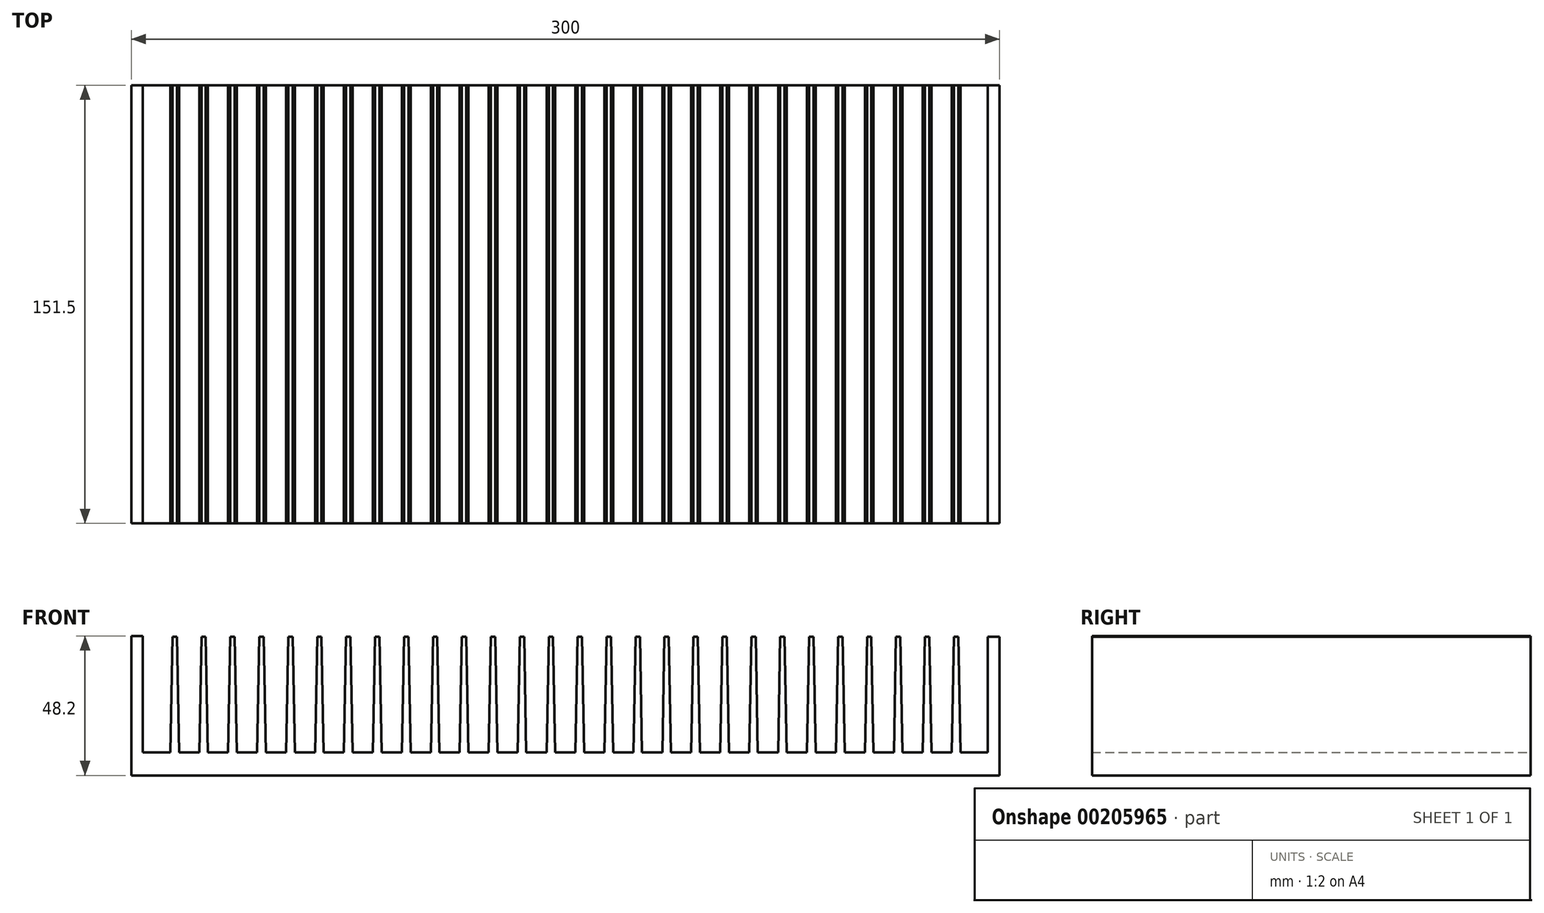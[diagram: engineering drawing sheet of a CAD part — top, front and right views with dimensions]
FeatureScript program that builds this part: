
annotation { "Feature Type Name" : "Feature", "Feature Type Description" : "" }
export const myFeature = defineFeature(function(context is Context, id is Id, definition is map)
    precondition{}
    {
        {
            var Q0;
            Q0=qCreatedBy(makeId("Front.planeOp"),FACE);
            var sketch = newSketch(context, id + "F0", { "sketchPlane" : qUnion([Q0])});
            skLineSegment(sketch, "E0", {"start": v(0, 0) * mm, "end": v(11.17, 0) * mm, "construction": true});
            skLineSegment(sketch, "E1", {"start": v(0, 0) * mm, "end": v(0, 12.82) * mm, "construction": true});
            skLineSegment(sketch, "E2", {"start": v(0, 48) * mm, "end": v(0.75, 48) * mm});
            skLineSegment(sketch, "E3", {"start": v(0.75, 48) * mm, "end": v(1.5, 8) * mm});
            skLineSegment(sketch, "E4", {"start": v(1.5, 8) * mm, "end": v(8.5, 8) * mm});
            skLineSegment(sketch, "E5", {"start": v(8.5, 8) * mm, "end": v(9.25, 48) * mm});
            skLineSegment(sketch, "E6", {"start": v(5, 23.61) * mm, "end": v(5, 0) * mm, "construction": true});
            skPoint(sketch, "E6.startSnap0", {"position": v(5, 8) * mm});
            skLineSegment(sketch, "E7", {"start": v(9.25, 48) * mm, "end": v(10, 48) * mm});
            skLineSegment(sketch, "E8.1.0.0", {"start": v(11.5, 8) * mm, "end": v(18.5, 8) * mm});
            skLineSegment(sketch, "E8.1.0.1", {"start": v(18.5, 8) * mm, "end": v(19.25, 48) * mm});
            skLineSegment(sketch, "E8.1.0.2", {"start": v(10.75, 48) * mm, "end": v(11.5, 8) * mm});
            skPoint(sketch, "E8.1.0.3", {"position": v(15, 8) * mm});
            skLineSegment(sketch, "E8.1.0.4", {"start": v(10, 48) * mm, "end": v(10.75, 48) * mm});
            skLineSegment(sketch, "E8.1.0.5", {"start": v(19.25, 48) * mm, "end": v(20, 48) * mm});
            skLineSegment(sketch, "E8.2.0.0", {"start": v(21.5, 8) * mm, "end": v(28.5, 8) * mm});
            skLineSegment(sketch, "E8.2.0.1", {"start": v(28.5, 8) * mm, "end": v(29.25, 48) * mm});
            skLineSegment(sketch, "E8.2.0.2", {"start": v(20.75, 48) * mm, "end": v(21.5, 8) * mm});
            skPoint(sketch, "E8.2.0.3", {"position": v(25, 8) * mm});
            skLineSegment(sketch, "E8.2.0.4", {"start": v(20, 48) * mm, "end": v(20.75, 48) * mm});
            skLineSegment(sketch, "E8.2.0.5", {"start": v(29.25, 48) * mm, "end": v(30, 48) * mm});
            skLineSegment(sketch, "E8.3.0.0", {"start": v(31.5, 8) * mm, "end": v(38.5, 8) * mm});
            skLineSegment(sketch, "E8.3.0.1", {"start": v(38.5, 8) * mm, "end": v(39.25, 48) * mm});
            skLineSegment(sketch, "E8.3.0.2", {"start": v(30.75, 48) * mm, "end": v(31.5, 8) * mm});
            skPoint(sketch, "E8.3.0.3", {"position": v(35, 8) * mm});
            skLineSegment(sketch, "E8.3.0.4", {"start": v(30, 48) * mm, "end": v(30.75, 48) * mm});
            skLineSegment(sketch, "E8.3.0.5", {"start": v(39.25, 48) * mm, "end": v(40, 48) * mm});
            skLineSegment(sketch, "E8.4.0.0", {"start": v(41.5, 8) * mm, "end": v(48.5, 8) * mm});
            skLineSegment(sketch, "E8.4.0.1", {"start": v(48.5, 8) * mm, "end": v(49.25, 48) * mm});
            skLineSegment(sketch, "E8.4.0.2", {"start": v(40.75, 48) * mm, "end": v(41.5, 8) * mm});
            skPoint(sketch, "E8.4.0.3", {"position": v(45, 8) * mm});
            skLineSegment(sketch, "E8.4.0.4", {"start": v(40, 48) * mm, "end": v(40.75, 48) * mm});
            skLineSegment(sketch, "E8.4.0.5", {"start": v(49.25, 48) * mm, "end": v(50, 48) * mm});
            skLineSegment(sketch, "E8.5.0.0", {"start": v(51.5, 8) * mm, "end": v(58.5, 8) * mm});
            skLineSegment(sketch, "E8.5.0.1", {"start": v(58.5, 8) * mm, "end": v(59.25, 48) * mm});
            skLineSegment(sketch, "E8.5.0.2", {"start": v(50.75, 48) * mm, "end": v(51.5, 8) * mm});
            skPoint(sketch, "E8.5.0.3", {"position": v(55, 8) * mm});
            skLineSegment(sketch, "E8.5.0.4", {"start": v(50, 48) * mm, "end": v(50.75, 48) * mm});
            skLineSegment(sketch, "E8.5.0.5", {"start": v(59.25, 48) * mm, "end": v(60, 48) * mm});
            skLineSegment(sketch, "E8.6.0.0", {"start": v(61.5, 8) * mm, "end": v(68.5, 8) * mm});
            skLineSegment(sketch, "E8.6.0.1", {"start": v(68.5, 8) * mm, "end": v(69.25, 48) * mm});
            skLineSegment(sketch, "E8.6.0.2", {"start": v(60.75, 48) * mm, "end": v(61.5, 8) * mm});
            skPoint(sketch, "E8.6.0.3", {"position": v(65, 8) * mm});
            skLineSegment(sketch, "E8.6.0.4", {"start": v(60, 48) * mm, "end": v(60.75, 48) * mm});
            skLineSegment(sketch, "E8.6.0.5", {"start": v(69.25, 48) * mm, "end": v(70, 48) * mm});
            skLineSegment(sketch, "E8.7.0.0", {"start": v(71.5, 8) * mm, "end": v(78.5, 8) * mm});
            skLineSegment(sketch, "E8.7.0.1", {"start": v(78.5, 8) * mm, "end": v(79.25, 48) * mm});
            skLineSegment(sketch, "E8.7.0.2", {"start": v(70.75, 48) * mm, "end": v(71.5, 8) * mm});
            skPoint(sketch, "E8.7.0.3", {"position": v(75, 8) * mm});
            skLineSegment(sketch, "E8.7.0.4", {"start": v(70, 48) * mm, "end": v(70.75, 48) * mm});
            skLineSegment(sketch, "E8.7.0.5", {"start": v(79.25, 48) * mm, "end": v(80, 48) * mm});
            skLineSegment(sketch, "E8.8.0.0", {"start": v(81.5, 8) * mm, "end": v(88.5, 8) * mm});
            skLineSegment(sketch, "E8.8.0.1", {"start": v(88.5, 8) * mm, "end": v(89.25, 48) * mm});
            skLineSegment(sketch, "E8.8.0.2", {"start": v(80.75, 48) * mm, "end": v(81.5, 8) * mm});
            skPoint(sketch, "E8.8.0.3", {"position": v(85, 8) * mm});
            skLineSegment(sketch, "E8.8.0.4", {"start": v(80, 48) * mm, "end": v(80.75, 48) * mm});
            skLineSegment(sketch, "E8.8.0.5", {"start": v(89.25, 48) * mm, "end": v(90, 48) * mm});
            skLineSegment(sketch, "E8.9.0.0", {"start": v(91.5, 8) * mm, "end": v(98.5, 8) * mm});
            skLineSegment(sketch, "E8.9.0.1", {"start": v(98.5, 8) * mm, "end": v(99.25, 48) * mm});
            skLineSegment(sketch, "E8.9.0.2", {"start": v(90.75, 48) * mm, "end": v(91.5, 8) * mm});
            skPoint(sketch, "E8.9.0.3", {"position": v(95, 8) * mm});
            skLineSegment(sketch, "E8.9.0.4", {"start": v(90, 48) * mm, "end": v(90.75, 48) * mm});
            skLineSegment(sketch, "E8.9.0.5", {"start": v(99.25, 48) * mm, "end": v(100, 48) * mm});
            skLineSegment(sketch, "E8.10.0.0", {"start": v(101.5, 8) * mm, "end": v(108.5, 8) * mm});
            skLineSegment(sketch, "E8.10.0.1", {"start": v(108.5, 8) * mm, "end": v(109.25, 48) * mm});
            skLineSegment(sketch, "E8.10.0.2", {"start": v(100.75, 48) * mm, "end": v(101.5, 8) * mm});
            skPoint(sketch, "E8.10.0.3", {"position": v(105, 8) * mm});
            skLineSegment(sketch, "E8.10.0.4", {"start": v(100, 48) * mm, "end": v(100.75, 48) * mm});
            skLineSegment(sketch, "E8.10.0.5", {"start": v(109.25, 48) * mm, "end": v(110, 48) * mm});
            skLineSegment(sketch, "E8.11.0.0", {"start": v(111.5, 8) * mm, "end": v(118.5, 8) * mm});
            skLineSegment(sketch, "E8.11.0.1", {"start": v(118.5, 8) * mm, "end": v(119.25, 48) * mm});
            skLineSegment(sketch, "E8.11.0.2", {"start": v(110.75, 48) * mm, "end": v(111.5, 8) * mm});
            skPoint(sketch, "E8.11.0.3", {"position": v(115, 8) * mm});
            skLineSegment(sketch, "E8.11.0.4", {"start": v(110, 48) * mm, "end": v(110.75, 48) * mm});
            skLineSegment(sketch, "E8.11.0.5", {"start": v(119.25, 48) * mm, "end": v(120, 48) * mm});
            skLineSegment(sketch, "E8.12.0.0", {"start": v(121.5, 8) * mm, "end": v(128.5, 8) * mm});
            skLineSegment(sketch, "E8.12.0.1", {"start": v(128.5, 8) * mm, "end": v(129.25, 48) * mm});
            skLineSegment(sketch, "E8.12.0.2", {"start": v(120.75, 48) * mm, "end": v(121.5, 8) * mm});
            skPoint(sketch, "E8.12.0.3", {"position": v(125, 8) * mm});
            skLineSegment(sketch, "E8.12.0.4", {"start": v(120, 48) * mm, "end": v(120.75, 48) * mm});
            skLineSegment(sketch, "E8.12.0.5", {"start": v(129.25, 48) * mm, "end": v(130, 48) * mm});
            skLineSegment(sketch, "E8.13.0.0", {"start": v(131.5, 8) * mm, "end": v(138.5, 8) * mm});
            skLineSegment(sketch, "E8.13.0.1", {"start": v(138.5, 8) * mm, "end": v(139.25, 48) * mm});
            skLineSegment(sketch, "E8.13.0.2", {"start": v(130.75, 48) * mm, "end": v(131.5, 8) * mm});
            skPoint(sketch, "E8.13.0.3", {"position": v(135, 8) * mm});
            skLineSegment(sketch, "E8.13.0.4", {"start": v(130, 48) * mm, "end": v(130.75, 48) * mm});
            skLineSegment(sketch, "E8.13.0.5", {"start": v(139.25, 48) * mm, "end": v(140, 48) * mm});
            skLineSegment(sketch, "E8.direction1", {"start": v(1.5, 8) * mm, "end": v(11.5, 8) * mm, "construction": true});
            skLineSegment(sketch, "E9.1.0.0", {"start": v(-9.25, 48) * mm, "end": v(-8.5, 8) * mm});
            skLineSegment(sketch, "E9.1.0.1", {"start": v(-8.5, 8) * mm, "end": v(-1.5, 8) * mm});
            skLineSegment(sketch, "E9.1.0.2", {"start": v(-1.5, 8) * mm, "end": v(-0.75, 48) * mm});
            skPoint(sketch, "E9.1.0.3", {"position": v(-5, 8) * mm});
            skLineSegment(sketch, "E9.1.0.4", {"start": v(-10, 48) * mm, "end": v(-9.25, 48) * mm});
            skLineSegment(sketch, "E9.1.0.5", {"start": v(-0.75, 48) * mm, "end": v(0, 48) * mm});
            skLineSegment(sketch, "E9.2.0.0", {"start": v(-19.25, 48) * mm, "end": v(-18.5, 8) * mm});
            skLineSegment(sketch, "E9.2.0.1", {"start": v(-18.5, 8) * mm, "end": v(-11.5, 8) * mm});
            skLineSegment(sketch, "E9.2.0.2", {"start": v(-11.5, 8) * mm, "end": v(-10.75, 48) * mm});
            skPoint(sketch, "E9.2.0.3", {"position": v(-15, 8) * mm});
            skLineSegment(sketch, "E9.2.0.4", {"start": v(-20, 48) * mm, "end": v(-19.25, 48) * mm});
            skLineSegment(sketch, "E9.2.0.5", {"start": v(-10.75, 48) * mm, "end": v(-10, 48) * mm});
            skLineSegment(sketch, "E9.direction1", {"start": v(-8.5, 8) * mm, "end": v(1.5, 8) * mm, "construction": true});
            skLineSegment(sketch, "E10.0.3.0", {"start": v(-29.25, 48) * mm, "end": v(-28.5, 8) * mm});
            skLineSegment(sketch, "E10.3.3.0", {"start": v(-28.5, 8) * mm, "end": v(-21.5, 8) * mm});
            skLineSegment(sketch, "E10.6.3.0", {"start": v(-21.5, 8) * mm, "end": v(-20.75, 48) * mm});
            skPoint(sketch, "E10.9.3.0", {"position": v(-25, 8) * mm});
            skLineSegment(sketch, "E10.10.3.0", {"start": v(-30, 48) * mm, "end": v(-29.25, 48) * mm});
            skLineSegment(sketch, "E10.13.3.0", {"start": v(-20.75, 48) * mm, "end": v(-20, 48) * mm});
            skLineSegment(sketch, "E10.0.4.0", {"start": v(-39.25, 48) * mm, "end": v(-38.5, 8) * mm});
            skLineSegment(sketch, "E10.3.4.0", {"start": v(-38.5, 8) * mm, "end": v(-31.5, 8) * mm});
            skLineSegment(sketch, "E10.6.4.0", {"start": v(-31.5, 8) * mm, "end": v(-30.75, 48) * mm});
            skPoint(sketch, "E10.9.4.0", {"position": v(-35, 8) * mm});
            skLineSegment(sketch, "E10.10.4.0", {"start": v(-40, 48) * mm, "end": v(-39.25, 48) * mm});
            skLineSegment(sketch, "E10.13.4.0", {"start": v(-30.75, 48) * mm, "end": v(-30, 48) * mm});
            skLineSegment(sketch, "E10.0.5.0", {"start": v(-49.25, 48) * mm, "end": v(-48.5, 8) * mm});
            skLineSegment(sketch, "E10.3.5.0", {"start": v(-48.5, 8) * mm, "end": v(-41.5, 8) * mm});
            skLineSegment(sketch, "E10.6.5.0", {"start": v(-41.5, 8) * mm, "end": v(-40.75, 48) * mm});
            skPoint(sketch, "E10.9.5.0", {"position": v(-45, 8) * mm});
            skLineSegment(sketch, "E10.10.5.0", {"start": v(-50, 48) * mm, "end": v(-49.25, 48) * mm});
            skLineSegment(sketch, "E10.13.5.0", {"start": v(-40.75, 48) * mm, "end": v(-40, 48) * mm});
            skLineSegment(sketch, "E10.0.6.0", {"start": v(-59.25, 48) * mm, "end": v(-58.5, 8) * mm});
            skLineSegment(sketch, "E10.3.6.0", {"start": v(-58.5, 8) * mm, "end": v(-51.5, 8) * mm});
            skLineSegment(sketch, "E10.6.6.0", {"start": v(-51.5, 8) * mm, "end": v(-50.75, 48) * mm});
            skPoint(sketch, "E10.9.6.0", {"position": v(-55, 8) * mm});
            skLineSegment(sketch, "E10.10.6.0", {"start": v(-60, 48) * mm, "end": v(-59.25, 48) * mm});
            skLineSegment(sketch, "E10.13.6.0", {"start": v(-50.75, 48) * mm, "end": v(-50, 48) * mm});
            skLineSegment(sketch, "E10.0.7.0", {"start": v(-69.25, 48) * mm, "end": v(-68.5, 8) * mm});
            skLineSegment(sketch, "E10.3.7.0", {"start": v(-68.5, 8) * mm, "end": v(-61.5, 8) * mm});
            skLineSegment(sketch, "E10.6.7.0", {"start": v(-61.5, 8) * mm, "end": v(-60.75, 48) * mm});
            skPoint(sketch, "E10.9.7.0", {"position": v(-65, 8) * mm});
            skLineSegment(sketch, "E10.10.7.0", {"start": v(-70, 48) * mm, "end": v(-69.25, 48) * mm});
            skLineSegment(sketch, "E10.13.7.0", {"start": v(-60.75, 48) * mm, "end": v(-60, 48) * mm});
            skLineSegment(sketch, "E10.0.8.0", {"start": v(-79.25, 48) * mm, "end": v(-78.5, 8) * mm});
            skLineSegment(sketch, "E10.3.8.0", {"start": v(-78.5, 8) * mm, "end": v(-71.5, 8) * mm});
            skLineSegment(sketch, "E10.6.8.0", {"start": v(-71.5, 8) * mm, "end": v(-70.75, 48) * mm});
            skPoint(sketch, "E10.9.8.0", {"position": v(-75, 8) * mm});
            skLineSegment(sketch, "E10.10.8.0", {"start": v(-80, 48) * mm, "end": v(-79.25, 48) * mm});
            skLineSegment(sketch, "E10.13.8.0", {"start": v(-70.75, 48) * mm, "end": v(-70, 48) * mm});
            skLineSegment(sketch, "E10.0.9.0", {"start": v(-89.25, 48) * mm, "end": v(-88.5, 8) * mm});
            skLineSegment(sketch, "E10.3.9.0", {"start": v(-88.5, 8) * mm, "end": v(-81.5, 8) * mm});
            skLineSegment(sketch, "E10.6.9.0", {"start": v(-81.5, 8) * mm, "end": v(-80.75, 48) * mm});
            skPoint(sketch, "E10.9.9.0", {"position": v(-85, 8) * mm});
            skLineSegment(sketch, "E10.10.9.0", {"start": v(-90, 48) * mm, "end": v(-89.25, 48) * mm});
            skLineSegment(sketch, "E10.13.9.0", {"start": v(-80.75, 48) * mm, "end": v(-80, 48) * mm});
            skLineSegment(sketch, "E10.0.10.0", {"start": v(-99.25, 48) * mm, "end": v(-98.5, 8) * mm});
            skLineSegment(sketch, "E10.3.10.0", {"start": v(-98.5, 8) * mm, "end": v(-91.5, 8) * mm});
            skLineSegment(sketch, "E10.6.10.0", {"start": v(-91.5, 8) * mm, "end": v(-90.75, 48) * mm});
            skPoint(sketch, "E10.9.10.0", {"position": v(-95, 8) * mm});
            skLineSegment(sketch, "E10.10.10.0", {"start": v(-100, 48) * mm, "end": v(-99.25, 48) * mm});
            skLineSegment(sketch, "E10.13.10.0", {"start": v(-90.75, 48) * mm, "end": v(-90, 48) * mm});
            skLineSegment(sketch, "E10.0.11.0", {"start": v(-109.25, 48) * mm, "end": v(-108.5, 8) * mm});
            skLineSegment(sketch, "E10.3.11.0", {"start": v(-108.5, 8) * mm, "end": v(-101.5, 8) * mm});
            skLineSegment(sketch, "E10.6.11.0", {"start": v(-101.5, 8) * mm, "end": v(-100.75, 48) * mm});
            skPoint(sketch, "E10.9.11.0", {"position": v(-105, 8) * mm});
            skLineSegment(sketch, "E10.10.11.0", {"start": v(-110, 48) * mm, "end": v(-109.25, 48) * mm});
            skLineSegment(sketch, "E10.13.11.0", {"start": v(-100.75, 48) * mm, "end": v(-100, 48) * mm});
            skLineSegment(sketch, "E10.0.12.0", {"start": v(-119.25, 48) * mm, "end": v(-118.5, 8) * mm});
            skLineSegment(sketch, "E10.3.12.0", {"start": v(-118.5, 8) * mm, "end": v(-111.5, 8) * mm});
            skLineSegment(sketch, "E10.6.12.0", {"start": v(-111.5, 8) * mm, "end": v(-110.75, 48) * mm});
            skPoint(sketch, "E10.9.12.0", {"position": v(-115, 8) * mm});
            skLineSegment(sketch, "E10.10.12.0", {"start": v(-120, 48) * mm, "end": v(-119.25, 48) * mm});
            skLineSegment(sketch, "E10.13.12.0", {"start": v(-110.75, 48) * mm, "end": v(-110, 48) * mm});
            skLineSegment(sketch, "E10.0.13.0", {"start": v(-129.25, 48) * mm, "end": v(-128.5, 8) * mm});
            skLineSegment(sketch, "E10.3.13.0", {"start": v(-128.5, 8) * mm, "end": v(-121.5, 8) * mm});
            skLineSegment(sketch, "E10.6.13.0", {"start": v(-121.5, 8) * mm, "end": v(-120.75, 48) * mm});
            skPoint(sketch, "E10.9.13.0", {"position": v(-125, 8) * mm});
            skLineSegment(sketch, "E10.10.13.0", {"start": v(-130, 48) * mm, "end": v(-129.25, 48) * mm});
            skLineSegment(sketch, "E10.13.13.0", {"start": v(-120.75, 48) * mm, "end": v(-120, 48) * mm});
            skLineSegment(sketch, "E11", {"start": v(-141, 48.2) * mm, "end": v(-145, 48.2) * mm});
            skLineSegment(sketch, "E12", {"start": v(-145, 48.2) * mm, "end": v(-145, 0) * mm});
            skLineSegment(sketch, "E13", {"start": v(-145, 0) * mm, "end": v(155, 0) * mm});
            skLineSegment(sketch, "E14", {"start": v(155, 0) * mm, "end": v(155, 48) * mm});
            skLineSegment(sketch, "E15", {"start": v(155, 48) * mm, "end": v(151, 48) * mm});
            skLineSegment(sketch, "E16", {"start": v(151, 8) * mm, "end": v(151, 48) * mm});
            skLineSegment(sketch, "E17", {"start": v(141.5, 8) * mm, "end": v(151, 8) * mm});
            skLineSegment(sketch, "E18", {"start": v(-131.5, 8) * mm, "end": v(-141, 8) * mm});
            skLineSegment(sketch, "E19", {"start": v(-141, 8) * mm, "end": v(-141, 48.2) * mm});
            skLineSegment(sketch, "E20", {"start": v(140, 48) * mm, "end": v(140.75, 48) * mm});
            skLineSegment(sketch, "E21", {"start": v(140.75, 48) * mm, "end": v(141.5, 8) * mm});
            skLineSegment(sketch, "E22", {"start": v(-130, 48) * mm, "end": v(-130.75, 48) * mm});
            skLineSegment(sketch, "E23", {"start": v(-130.75, 48) * mm, "end": v(-131.5, 8) * mm});
            skSolve(sketch);
        }
        {
            var Q0;
            Q0 = qSketchRegion(id + "F0", true);
            extrude(context, id + "F1", {"entities" : qUnion([Q0]), "depth" : 151.5 * mm});
        }
    });
